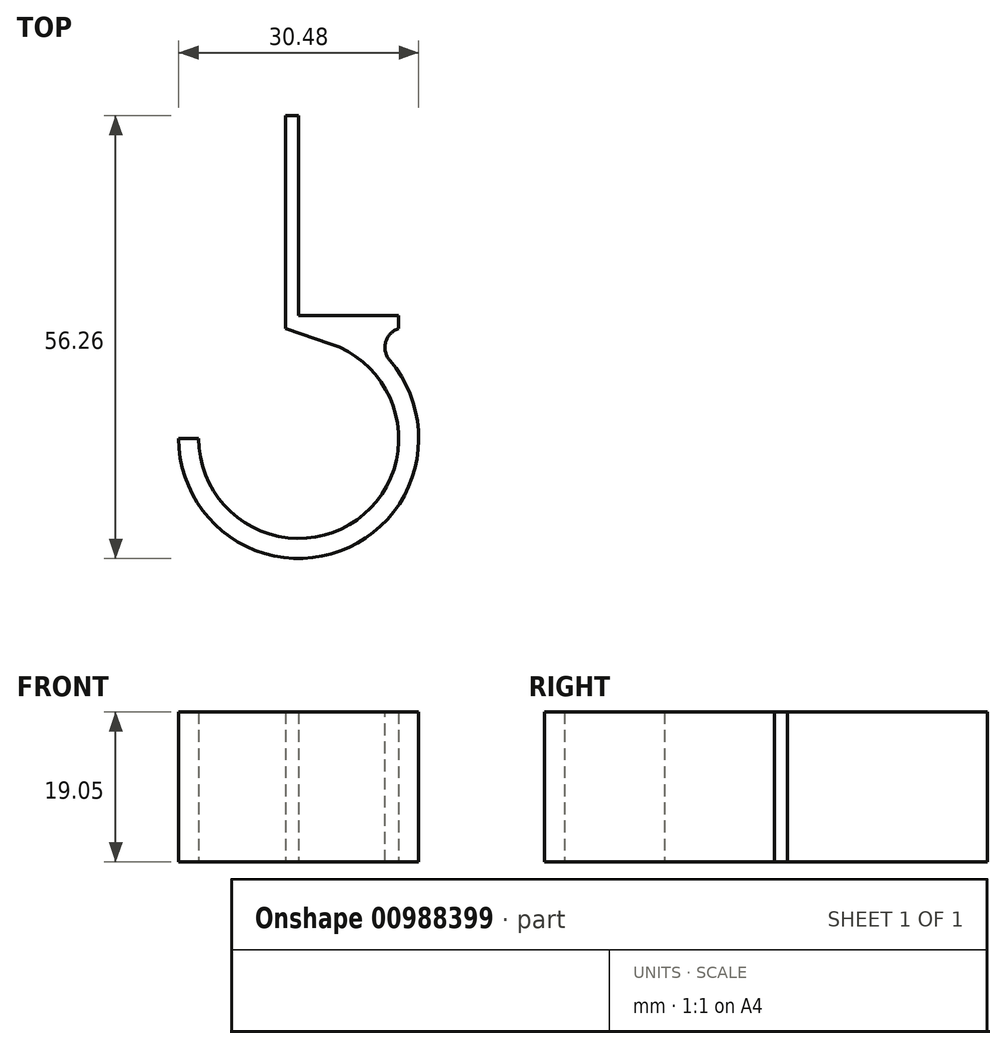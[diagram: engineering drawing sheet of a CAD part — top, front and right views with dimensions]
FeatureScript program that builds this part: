
annotation { "Feature Type Name" : "Feature", "Feature Type Description" : "" }
export const myFeature = defineFeature(function(context is Context, id is Id, definition is map)
    precondition{}
    {
        {
            var Q0;
            Q0=qCreatedBy(makeId("Top.planeOp"),FACE);
            var sketch = newSketch(context, id + "F0", { "sketchPlane" : qUnion([Q0])});
            skLineSegment(sketch, "E0.bottom", {"start": v(0, 0) * mm, "end": v(12.7, 0) * mm});
            skLineSegment(sketch, "E0.top", {"start": v(0, -1.65) * mm, "end": v(12.7, -1.65) * mm});
            skLineSegment(sketch, "E0.left", {"start": v(0, 0) * mm, "end": v(0, -1.65) * mm});
            skLineSegment(sketch, "E0.right", {"start": v(12.7, 0) * mm, "end": v(12.7, -1.65) * mm});
            skLineSegment(sketch, "E1.bottom", {"start": v(0, -1.65) * mm, "end": v(-1.65, -1.65) * mm});
            skLineSegment(sketch, "E1.top", {"start": v(0, 25.4) * mm, "end": v(-1.65, 25.4) * mm});
            skLineSegment(sketch, "E1.left", {"start": v(0, -1.65) * mm, "end": v(0, 25.4) * mm});
            skLineSegment(sketch, "E1.right", {"start": v(-1.65, -1.65) * mm, "end": v(-1.65, 25.4) * mm});
            skArc(sketch, "E2", {"start": v(-12.7, -15.62) * mm, "mid": v(7.4, -25.94) * mm, "end": v(4.08, -3.6) * mm});
            skArc(sketch, "E3.0", {"start": v(-15.24, -15.62) * mm, "mid": v(7.49, -28.9) * mm, "end": v(7.89, -2.58) * mm});
            skLineSegment(sketch, "E4", {"start": v(-12.7, -15.62) * mm, "end": v(-15.24, -15.62) * mm});
            skLineSegment(sketch, "E5", {"start": v(6.35, -1.65) * mm, "end": v(7.89, -2.58) * mm});
            skLineSegment(sketch, "E6", {"start": v(-1.65, -1.65) * mm, "end": v(4.08, -3.6) * mm});
            skSolve(sketch);
        }
        {
            var Q0;
            Q0 = qSketchRegion(id + "F0", true);
            extrude(context, id + "F1", {"entities" : qUnion([Q0]), "depth" : 19.05 * mm, "offsetDistance" : 25.4 * mm});
        }
        {
            var Q0;
            Q0=makeQuery(id+"F1.opExtrude","SWEPT_EDGE",EDGE,{"disambiguationData":[OSD([sQuery(id+"F0.wireOp",EDGE,"E0.top"),sQuery(id+"F0.wireOp",EDGE,"E5")])]});
            fillet(context, id + "F2", {"entities" : qUnion([Q0]), "radius" : 2.54 * mm, "tangentPropagation" : true, "allowEdgeOverflow" : false});
        }
    });
